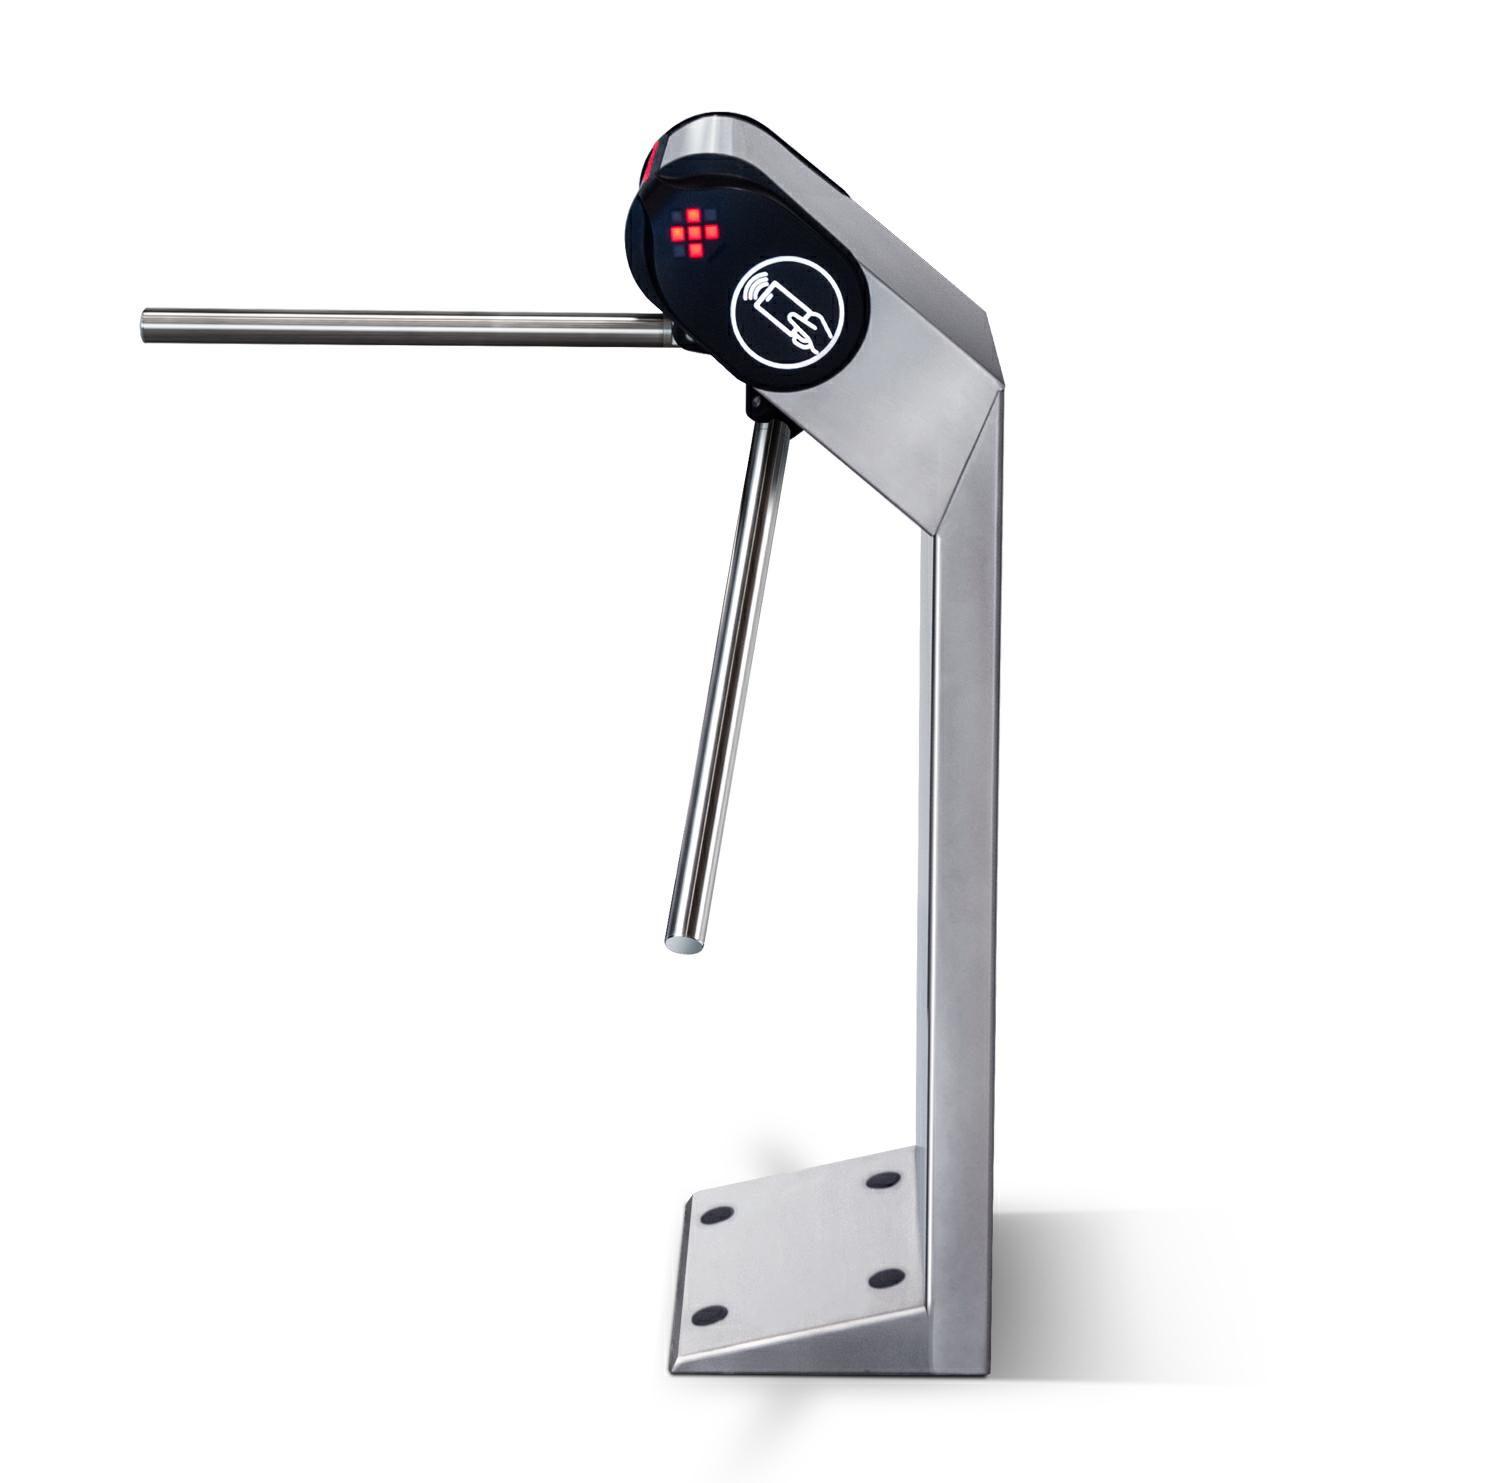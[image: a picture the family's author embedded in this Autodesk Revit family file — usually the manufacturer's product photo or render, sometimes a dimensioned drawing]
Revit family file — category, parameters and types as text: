
# Revit family: Турникет трипод PERCo_TTR-08А
name_source: partatom
category: Оборудование
units: mm (PartAtom-declared; Revit-internal decimal feet)

## family parameters
Всегда вертикально = Да
Классификация = Нет
На основе рабочей плоскости = Нет
Общий = Нет
При загрузке вырезать с полостями = Нет
Размер круглого соединителя = Использовать диаметр
Тип детали = Нормальный
Точка расчета площади = Нет

## types (1)
- TTR-08А
    ADSK_URL страницы изделия = https://www.perco.ru
    ADSK_Единица измерения = шт.
    ADSK_Завод-изготовитель = PERCo
    ADSK_Количество = 1
    ADSK_Масса_Текст = не более 37 кг
    ADSK_Материал наименование = Корпус  турникета выполнен из высококачественной нержавеющей стали со вставками из АБС-пластика, планки из нержавеющей стали
    ADSK_Наименование = Турникет эл/мех PERCo-TTR-08A с автоматическими преграждающими планками Антипаника, для эксплуатации на открытом воздухе
    ADSK_Наименование краткое = Турникет TTR-08А
    ADSK_Напряжение = 12 В
    ADSK_Номинальная мощность = 72 Вт
    ADSK_Ток = 6 А
    Встраивание считывателей внутрь = Да
    Габаритные размеры (длина×ширина×высота) = 777×798×1084 мм
    Габаритные размеры контроллера для встраивания в нишу = не более 240×200×35 мм
    Габаритные размеры считывателя для встраивания в ниши = не более 145×90×25 мм
    Длина планки = 538 мм
    Изображение типоразмера = <Нет>
    Материал планок = Нержавейка
    Окраска турникета = Нержавеющая сталь
    Основание планок = Черный
    Подключение к электросети = 220 В
    Пропускная способность = 30 чел./мин
    Степень защиты оболочки = IP54
    Стоимость = 0 $
    Температура использования = от –20°С до +50°С
    Цвет = Нержавейка
    Ширна зоны прохода = 500 мм.
